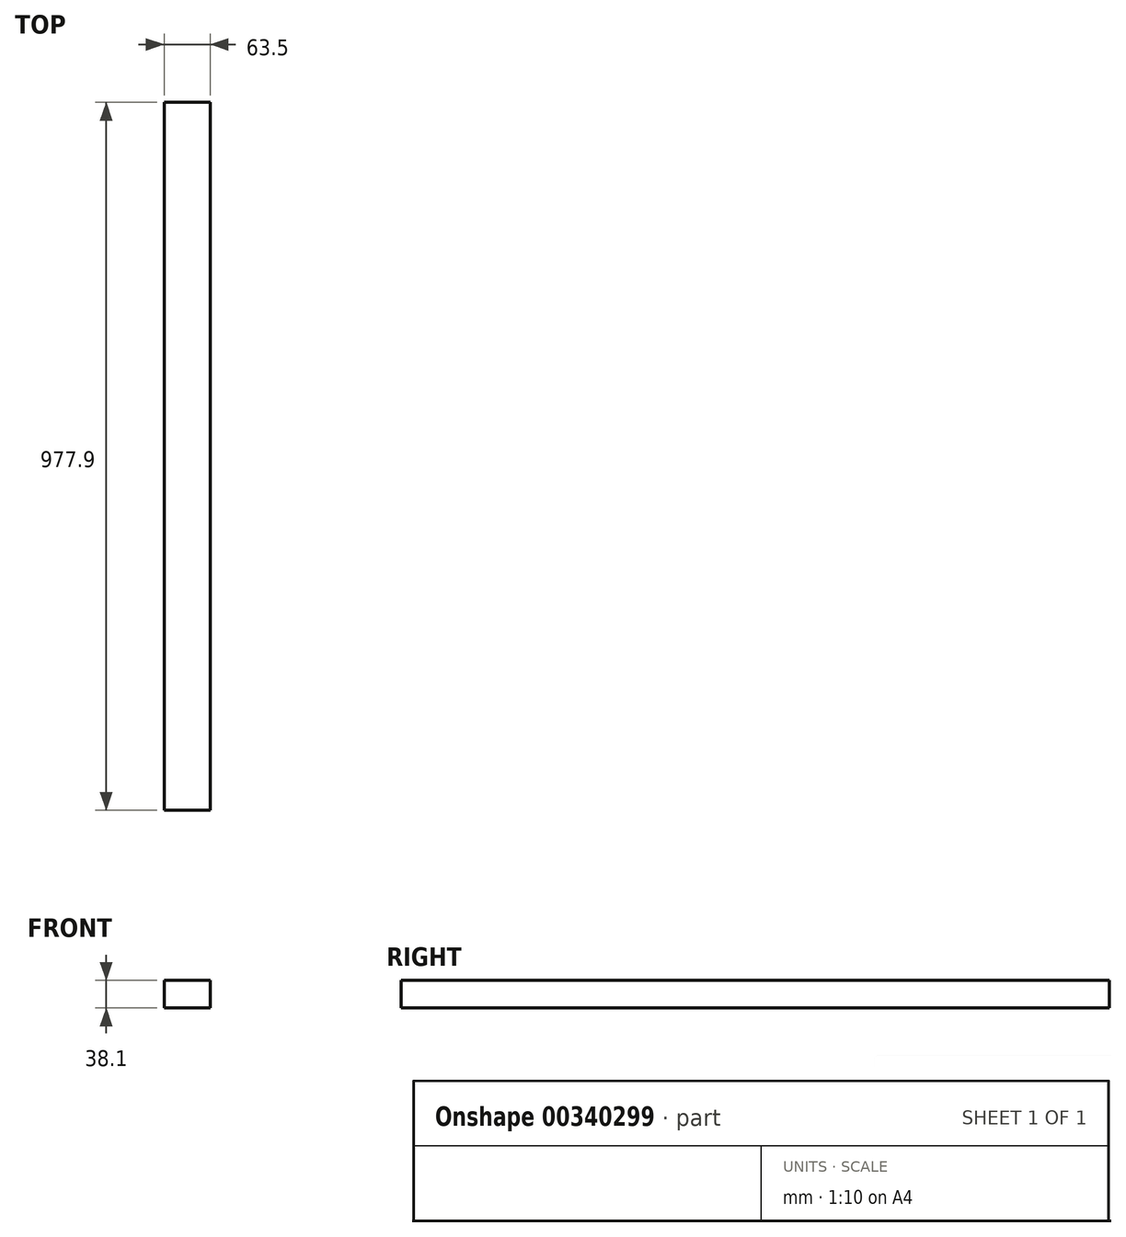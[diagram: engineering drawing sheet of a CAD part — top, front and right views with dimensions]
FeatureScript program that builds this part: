
annotation { "Feature Type Name" : "Feature", "Feature Type Description" : "" }
export const myFeature = defineFeature(function(context is Context, id is Id, definition is map)
    precondition{}
    {
        {
            var Q0;
            Q0=qCreatedBy(makeId("Front.planeOp"),FACE);
            var sketch = newSketch(context, id + "F0", { "sketchPlane" : qUnion([Q0])});
            skLineSegment(sketch, "E0.bottom", {"start": v(35.64, -16.66) * mm, "end": v(-27.86, -16.66) * mm});
            skLineSegment(sketch, "E0.top", {"start": v(35.64, 21.44) * mm, "end": v(-27.86, 21.44) * mm});
            skLineSegment(sketch, "E0.left", {"start": v(35.64, -16.66) * mm, "end": v(35.64, 21.44) * mm});
            skLineSegment(sketch, "E0.right", {"start": v(-27.86, -16.66) * mm, "end": v(-27.86, 21.44) * mm});
            skPoint(sketch, "E0.middle", {"position": v(3.9, 2.4) * mm});
            skSolve(sketch);
        }
        {
            var Q0;
            Q0=qSketchRegion(id+"F0",true);
            extrude(context, id + "F1", {"entities" : qUnion([Q0]), "depth" : 977.9 * mm});
        }
    });
